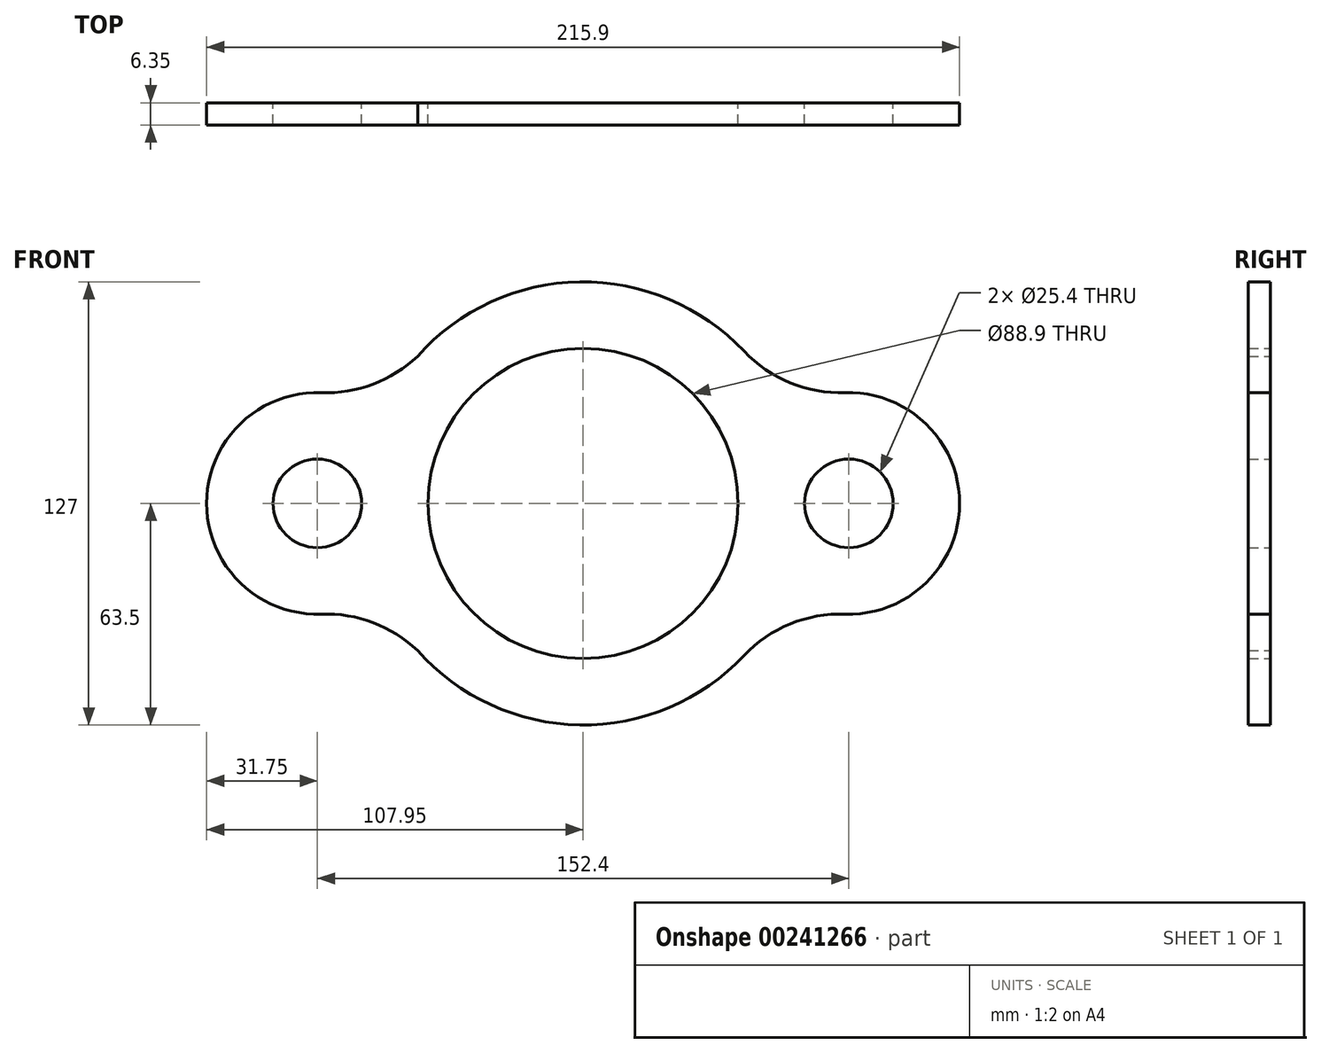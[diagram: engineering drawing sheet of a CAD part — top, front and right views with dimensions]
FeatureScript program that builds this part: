
annotation { "Feature Type Name" : "Feature", "Feature Type Description" : "" }
export const myFeature = defineFeature(function(context is Context, id is Id, definition is map)
    precondition{}
    {
        {
            var Q0;
            Q0=qCreatedBy(makeId("Front.planeOp"),FACE);
            var sketch = newSketch(context, id + "F0", { "sketchPlane" : qUnion([Q0])});
            skCircle(sketch, "E0", {"center": v(0, 0) * mm, "radius": 44.45 * mm});
            skLineSegment(sketch, "E1", {"start": v(0, -74.97) * mm, "end": v(-76.2, -74.97) * mm, "construction": true});
            skArc(sketch, "E2", {"start": v(-75.07, 31.73) * mm, "mid": v(-107.95, 0) * mm, "end": v(-75.07, -31.73) * mm});
            skLineSegment(sketch, "E3", {"start": v(0, -74.97) * mm, "end": v(76.2, -74.97) * mm, "construction": true});
            skCircle(sketch, "E4", {"center": v(-76.2, 0) * mm, "radius": 12.7 * mm});
            skCircle(sketch, "E5", {"center": v(76.2, 0) * mm, "radius": 12.7 * mm});
            skLineSegment(sketch, "E6", {"start": v(-76.2, -12.7) * mm, "end": v(-76.2, 12.7) * mm, "construction": true});
            skArc(sketch, "E7.filletArc", {"start": v(-47.46, -42.2) * mm, "mid": v(-60.2, -34.18) * mm, "end": v(-75.07, -31.73) * mm});
            skArc(sketch, "E8.filletArc", {"start": v(-75.07, 31.73) * mm, "mid": v(-60.2, 34.18) * mm, "end": v(-47.46, 42.2) * mm});
            skArc(sketch, "E9", {"start": v(46.14, 43.63) * mm, "mid": v(-0.98, 63.5) * mm, "end": v(-47.46, 42.2) * mm});
            skArc(sketch, "E10", {"start": v(75.12, -31.73) * mm, "mid": v(107.95, 0) * mm, "end": v(75.12, 31.73) * mm});
            skArc(sketch, "E11.trimOffspring", {"start": v(-47.46, -42.2) * mm, "mid": v(-0.98, -63.5) * mm, "end": v(46.14, -43.63) * mm});
            skArc(sketch, "E12.filletArc", {"start": v(46.14, 43.63) * mm, "mid": v(59.35, 34.56) * mm, "end": v(75.12, 31.73) * mm});
            skArc(sketch, "E13.filletArc", {"start": v(75.12, -31.73) * mm, "mid": v(59.35, -34.56) * mm, "end": v(46.14, -43.63) * mm});
            skSolve(sketch);
        }
        {
            var Q0;
            Q0=makeQuery(id+"F0.imprint","IMPRINT",FACE,{"disambiguationData":[TD([[makeQuery(id+"F0.imprint","IMPRINT",EDGE,{"derivedFrom":sQuery(id+"F0.wireOp",EDGE,"E0")}),-1.0]])]});
            extrude(context, id + "F1", {"entities" : qUnion([Q0]), "depth" : 6.35 * mm});
        }
    });
